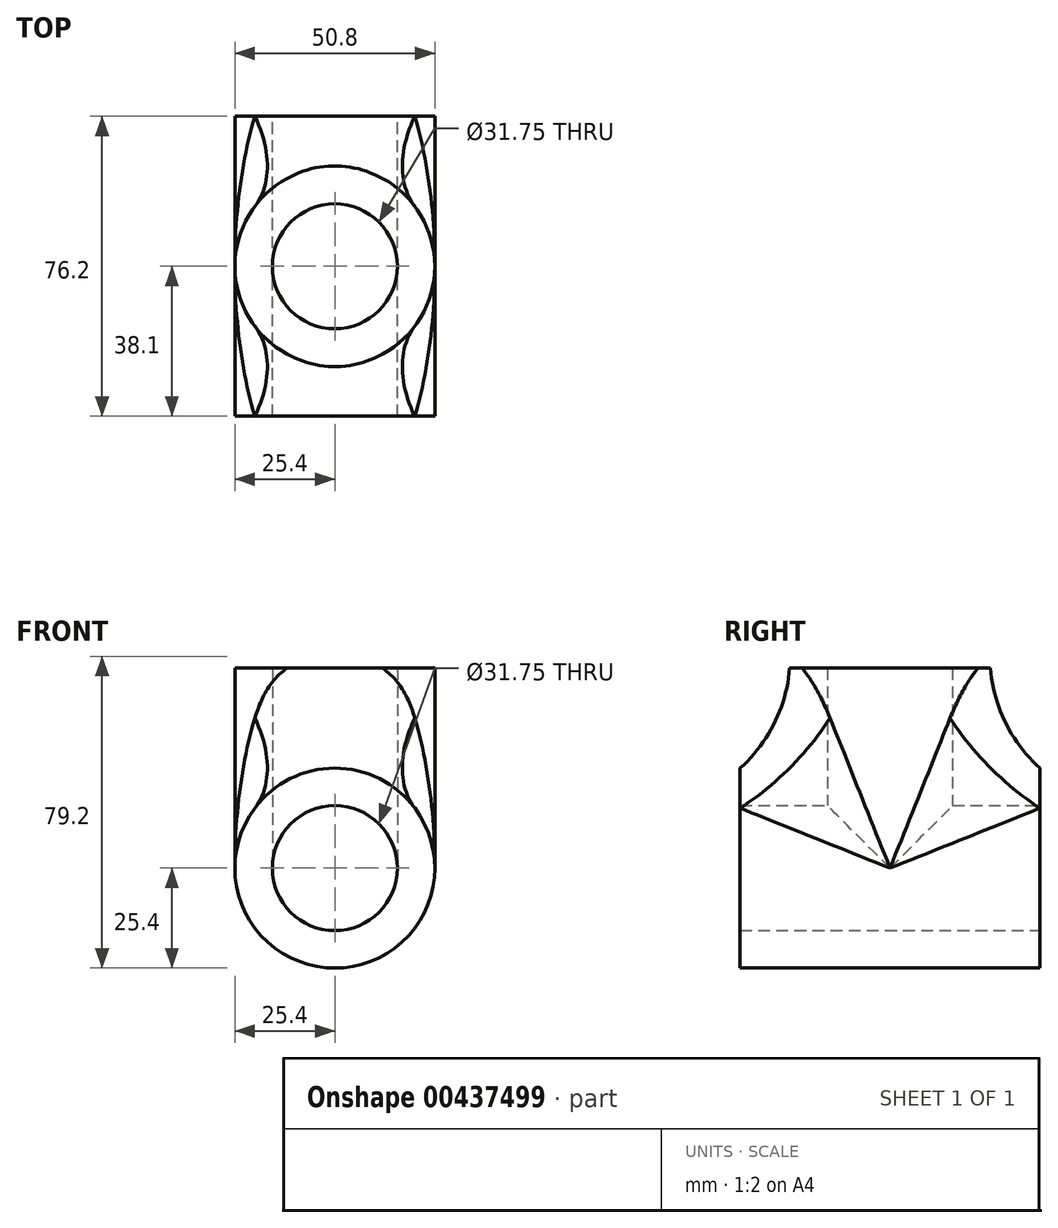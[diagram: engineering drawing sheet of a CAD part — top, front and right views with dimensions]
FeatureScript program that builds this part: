
annotation { "Feature Type Name" : "Feature", "Feature Type Description" : "" }
export const myFeature = defineFeature(function(context is Context, id is Id, definition is map)
    precondition{}
    {
        {
            var Q0;
            Q0=qCreatedBy(makeId("Front.planeOp"),FACE);
            var sketch = newSketch(context, id + "F0", { "sketchPlane" : qUnion([Q0])});
            skCircle(sketch, "E0", {"center": v(0, 0) * mm, "radius": 15.88 * mm});
            skCircle(sketch, "E1", {"center": v(0, 0) * mm, "radius": 25.4 * mm});
            skSolve(sketch);
        }
        {
            var Q0;
            Q0 = qSketchRegion(id + "F0", true);
            extrude(context, id + "F1", {"entities" : qUnion([Q0]), "depth" : 38.1 * mm, "offsetDistance" : 25.4 * mm, "hasSecondDirection" : true, "secondDirectionOppositeDirection" : true, "secondDirectionDepth" : 38.1 * mm});
        }
        {
            var Q0;
            Q0=qCreatedBy(makeId("Top.planeOp"),FACE);
            var sketch = newSketch(context, id + "F2", { "sketchPlane" : qUnion([Q0])});
            skCircle(sketch, "E2", {"center": v(0, 0) * mm, "radius": 25.4 * mm});
            skCircle(sketch, "E3", {"center": v(0, 0) * mm, "radius": 15.88 * mm});
            skSolve(sketch);
        }
        {
            var Q0;
            Q0 = qSketchRegion(id + "F2", true);
            extrude(context, id + "F3", {"entities" : qUnion([Q0]), "operationType" : NewBodyOperationType.ADD, "depth" : 50.8 * mm, "offsetDistance" : 25.4 * mm});
        }
        {
            var Q0;
            Q0=makeQuery(id+"F1.opExtrude","CAP_FACE",FACE,{"disambiguationData":[OSD([sQuery(id+"F0.wireOp",EDGE,"E0"),sQuery(id+"F0.wireOp",EDGE,"E1")])],"isStart":true});
            var sketch = newSketch(context, id + "F4", { "sketchPlane" : qUnion([Q0])});
            skCircle(sketch, "E4", {"center": v(0, 0) * mm, "radius": 15.88 * mm});
            skSolve(sketch);
        }
        {
            var Q0;
            Q0 = qSketchRegion(id + "F4", true);
            extrude(context, id + "F5", {"entities" : qUnion([Q0]), "operationType" : NewBodyOperationType.REMOVE, "oppositeDirection" : true, "depth" : 104.9 * mm, "offsetDistance" : 25.4 * mm});
        }
        {
            var Q0;
            Q0=makeQuery(id+"F3.boolean.opBoolean","INTERSECT",EDGE,{"disambiguationData":[OD(1.0)],"derivedFrom":[makeQuery(id+"F1.opExtrude","SWEPT_FACE",FACE,{"disambiguationData":[OSD([sQuery(id+"F0.wireOp",EDGE,"E1")])]}),makeQuery(id+"F3.opExtrude","SWEPT_FACE",FACE,{"disambiguationData":[OSD([sQuery(id+"F2.wireOp",EDGE,"E2")])]})]});
            var Q1;
            Q1=makeQuery(id+"F3.boolean.opBoolean","INTERSECT",EDGE,{"disambiguationData":[OD(0.0)],"derivedFrom":[makeQuery(id+"F1.opExtrude","SWEPT_FACE",FACE,{"disambiguationData":[OSD([sQuery(id+"F0.wireOp",EDGE,"E1")])]}),makeQuery(id+"F3.opExtrude","SWEPT_FACE",FACE,{"disambiguationData":[OSD([sQuery(id+"F2.wireOp",EDGE,"E2")])]})]});
            fillet(context, id + "F6", {"entities" : qUnion([Q0, Q1]), "radius" : 38.1 * mm, "tangentPropagation" : true, "allowEdgeOverflow" : false});
        }
        {
            var Q0;
            Q0=makeQuery(id+"F3.opExtrude","CAP_FACE",FACE,{"disambiguationData":[OSD([sQuery(id+"F2.wireOp",EDGE,"E2"),sQuery(id+"F2.wireOp",EDGE,"E3")])],"isStart":false});
            var sketch = newSketch(context, id + "F7", { "sketchPlane" : qUnion([Q0])});
            skCircle(sketch, "E5", {"center": v(0, 0) * mm, "radius": 15.88 * mm});
            skSolve(sketch);
        }
        {
            var Q0;
            Q0 = qSketchRegion(id + "F7", true);
            extrude(context, id + "F8", {"entities" : qUnion([Q0]), "operationType" : NewBodyOperationType.REMOVE, "oppositeDirection" : true, "depth" : 50.8 * mm, "offsetDistance" : 25.4 * mm});
        }
    });
